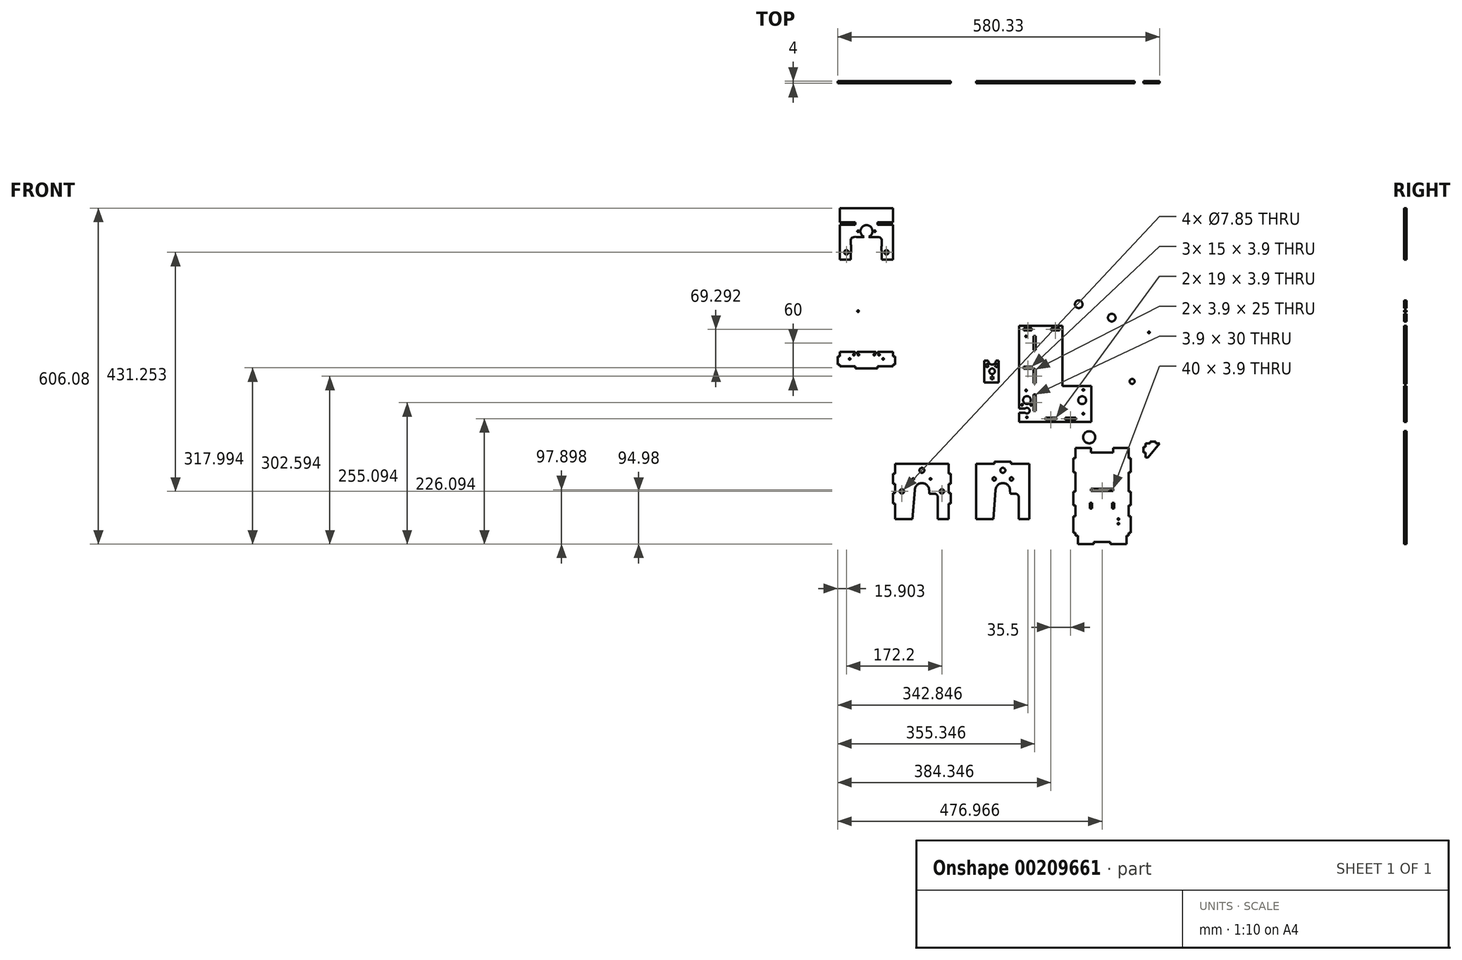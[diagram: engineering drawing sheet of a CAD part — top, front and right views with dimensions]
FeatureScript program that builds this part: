
annotation { "Feature Type Name" : "Feature", "Feature Type Description" : "" }
export const myFeature = defineFeature(function(context is Context, id is Id, definition is map)
    precondition{}
    {
        {
            var Q0;
            Q0=qCreatedBy(makeId("Front.planeOp"),FACE);
            var sketch = newSketch(context, id + "F0", { "sketchPlane" : qUnion([Q0])});
            skLineSegment(sketch, "E0", {"start": v(-63.43, -22.95) * mm, "end": v(-63.43, -82.95) * mm});
            skLineSegment(sketch, "E1", {"start": v(-63.43, -82.95) * mm, "end": v(66.57, -82.95) * mm});
            skLineSegment(sketch, "E2", {"start": v(66.57, -82.95) * mm, "end": v(66.56, -50.54) * mm});
            skLineSegment(sketch, "E3", {"start": v(66.56, -50.54) * mm, "end": v(66.57, -17.95) * mm});
            skLineSegment(sketch, "E4", {"start": v(66.57, -17.95) * mm, "end": v(29.57, -17.95) * mm});
            skLineSegment(sketch, "E5", {"start": v(-37.38, -62.95) * mm, "end": v(-37.38, -32.95) * mm});
            skLineSegment(sketch, "E6", {"start": v(-37.38, -32.95) * mm, "end": v(-33.48, -32.95) * mm});
            skLineSegment(sketch, "E7", {"start": v(-33.48, -32.95) * mm, "end": v(-33.48, -62.95) * mm});
            skLineSegment(sketch, "E8", {"start": v(-33.48, -62.95) * mm, "end": v(-37.38, -62.95) * mm});
            skLineSegment(sketch, "E9", {"start": v(-63.43, -22.95) * mm, "end": v(-63.43, 90.44) * mm});
            skLineSegment(sketch, "E10", {"start": v(-37.38, -12.95) * mm, "end": v(-37.38, 12.05) * mm});
            skLineSegment(sketch, "E11", {"start": v(-37.38, 12.05) * mm, "end": v(-33.48, 12.05) * mm});
            skLineSegment(sketch, "E12", {"start": v(-33.48, 12.05) * mm, "end": v(-33.48, -12.95) * mm});
            skLineSegment(sketch, "E13", {"start": v(-33.48, -12.95) * mm, "end": v(-37.38, -12.95) * mm});
            skLineSegment(sketch, "E14", {"start": v(-63.43, 90.44) * mm, "end": v(14.57, 90.44) * mm});
            skLineSegment(sketch, "E15", {"start": v(9.41, 86.2) * mm, "end": v(9.41, 82.3) * mm});
            skLineSegment(sketch, "E16", {"start": v(9.41, 82.3) * mm, "end": v(-5.59, 82.3) * mm});
            skLineSegment(sketch, "E17", {"start": v(-5.59, 82.3) * mm, "end": v(-5.59, 86.2) * mm});
            skLineSegment(sketch, "E18", {"start": v(-5.59, 86.2) * mm, "end": v(9.41, 86.2) * mm});
            skCircle(sketch, "E19", {"center": v(-50.93, -25.95) * mm, "radius": 1.4 * mm});
            skCircle(sketch, "E20", {"center": v(52.21, -24.95) * mm, "radius": 1.5 * mm});
            skCircle(sketch, "E21", {"center": v(52.21, -67.95) * mm, "radius": 1.5 * mm});
            skCircle(sketch, "E22", {"center": v(-49.43, -74.35) * mm, "radius": 1.4 * mm});
            skLineSegment(sketch, "E23", {"start": v(-40.43, 16.9) * mm, "end": v(-40.43, 13) * mm});
            skLineSegment(sketch, "E24", {"start": v(-40.43, 13) * mm, "end": v(-55.43, 13) * mm});
            skLineSegment(sketch, "E25", {"start": v(-55.43, 13) * mm, "end": v(-55.43, 16.9) * mm});
            skLineSegment(sketch, "E26", {"start": v(-55.43, 16.9) * mm, "end": v(-40.43, 16.9) * mm});
            skLineSegment(sketch, "E27", {"start": v(-37.38, 47.05) * mm, "end": v(-37.38, 72.05) * mm});
            skLineSegment(sketch, "E28", {"start": v(-37.38, 72.05) * mm, "end": v(-33.48, 72.05) * mm});
            skLineSegment(sketch, "E29", {"start": v(-33.48, 72.05) * mm, "end": v(-33.48, 47.05) * mm});
            skLineSegment(sketch, "E30", {"start": v(-33.48, 47.05) * mm, "end": v(-37.38, 47.05) * mm});
            skCircle(sketch, "E31", {"center": v(-50.93, 71.63) * mm, "radius": 1.4 * mm});
            skLineSegment(sketch, "E32", {"start": v(-40.43, 86.2) * mm, "end": v(-40.43, 82.3) * mm});
            skLineSegment(sketch, "E33", {"start": v(-40.43, 82.3) * mm, "end": v(-55.43, 82.3) * mm});
            skLineSegment(sketch, "E34", {"start": v(-55.43, 82.3) * mm, "end": v(-55.43, 86.2) * mm});
            skLineSegment(sketch, "E35", {"start": v(-55.43, 86.2) * mm, "end": v(-40.43, 86.2) * mm});
            skCircle(sketch, "E36", {"center": v(52.21, -24.95) * mm, "radius": 1.4 * mm});
            skCircle(sketch, "E37", {"center": v(52.21, -67.95) * mm, "radius": 1.4 * mm});
            skLineSegment(sketch, "E38", {"start": v(29.57, -17.95) * mm, "end": v(19.57, -17.95) * mm});
            skLineSegment(sketch, "E39", {"start": v(19.57, -17.95) * mm, "end": v(14.57, -17.95) * mm});
            skLineSegment(sketch, "E40", {"start": v(14.57, -17.95) * mm, "end": v(14.57, 90.44) * mm});
            skLineSegment(sketch, "E41", {"start": v(3.07, -78.9) * mm, "end": v(-15.93, -78.9) * mm});
            skLineSegment(sketch, "E42", {"start": v(-15.93, -78.9) * mm, "end": v(-15.93, -75) * mm});
            skLineSegment(sketch, "E43", {"start": v(-15.93, -75) * mm, "end": v(3.07, -75) * mm});
            skLineSegment(sketch, "E44", {"start": v(3.07, -75) * mm, "end": v(3.07, -78.9) * mm});
            skLineSegment(sketch, "E45", {"start": v(38.57, -78.9) * mm, "end": v(19.57, -78.9) * mm});
            skLineSegment(sketch, "E46", {"start": v(19.57, -78.9) * mm, "end": v(19.57, -75) * mm});
            skLineSegment(sketch, "E47", {"start": v(19.57, -75) * mm, "end": v(38.57, -75) * mm});
            skLineSegment(sketch, "E48", {"start": v(38.57, -75) * mm, "end": v(38.57, -78.9) * mm});
            skCircle(sketch, "E49", {"center": v(-49.43, -43.45) * mm, "radius": 7.1 * mm});
            skCircle(sketch, "E50", {"center": v(-49.43, -62.45) * mm, "radius": 5 * mm});
            skLineSegment(sketch, "E51", {"start": v(-52.43, -58.45) * mm, "end": v(-63.43, -58.45) * mm});
            skLineSegment(sketch, "E52", {"start": v(-52.43, -66.45) * mm, "end": v(-63.43, -66.45) * mm});
            skCircle(sketch, "E53", {"center": v(50.08, -43.54) * mm, "radius": 7.1 * mm});
            skCircle(sketch, "E54", {"center": v(-58.5, -51.92) * mm, "radius": 1.4 * mm});
            skCircle(sketch, "E55", {"center": v(-41.8, -51.92) * mm, "radius": 1.4 * mm});
            skSolve(sketch);
        }
        {
            var Q0;
            Q0=qCreatedBy(makeId("Front.planeOp"),FACE);
            var sketch = newSketch(context, id + "F1", { "sketchPlane" : qUnion([Q0])});
            skLineSegment(sketch, "E56", {"start": v(120.16, -22.83) * mm, "end": v(160.16, -22.83) * mm});
            skCircle(sketch, "E57", {"center": v(140.16, -9.68) * mm, "radius": 4.5 * mm});
            skLineSegment(sketch, "E58", {"start": v(115.16, -22.83) * mm, "end": v(165.16, -22.83) * mm});
            skLineSegment(sketch, "E59", {"start": v(165.16, 2.17) * mm, "end": v(162.16, 2.17) * mm});
            skLineSegment(sketch, "E60", {"start": v(118.16, 2.17) * mm, "end": v(115.16, 2.17) * mm});
            skLineSegment(sketch, "E61", {"start": v(120.16, 6.17) * mm, "end": v(160.16, 6.17) * mm});
            skLineSegment(sketch, "E62", {"start": v(115.16, -22.83) * mm, "end": v(115.16, -9.83) * mm});
            skLineSegment(sketch, "E63", {"start": v(120.16, 6.17) * mm, "end": v(120.16, 2.17) * mm});
            skLineSegment(sketch, "E64", {"start": v(160.16, 6.17) * mm, "end": v(160.16, 2.17) * mm});
            skLineSegment(sketch, "E65", {"start": v(118.16, 2.17) * mm, "end": v(120.16, 2.17) * mm});
            skLineSegment(sketch, "E66", {"start": v(162.16, 2.17) * mm, "end": v(160.16, 2.17) * mm});
            skLineSegment(sketch, "E67", {"start": v(115.16, -9.83) * mm, "end": v(115.16, 2.17) * mm});
            skLineSegment(sketch, "E68", {"start": v(115.16, -22.83) * mm, "end": v(115.16, 2.17) * mm});
            skLineSegment(sketch, "E69", {"start": v(165.16, -22.83) * mm, "end": v(165.16, 2.17) * mm});
            skCircle(sketch, "E70", {"center": v(124.99, -15.63) * mm, "radius": 1.4 * mm});
            skCircle(sketch, "E71", {"center": v(155.33, -3.77) * mm, "radius": 1.4 * mm});
            skSolve(sketch);
        }
        {
            var Q0;
            {var subQ5=sQuery(id+"F0.wireOp",EDGE,"E1");Q0=makeQuery(id+"F0.imprint","IMPRINT",FACE,{"disambiguationData":[TD([[makeQuery(id+"F0.imprint","IMPRINT",EDGE,{"derivedFrom":subQ5}),1.0]])]});}
            extrude(context, id + "F2", {"entities" : qUnion([Q0]), "depth" : 4 * mm});
        }
        {
            var Q0;
            Q0=makeQuery(id+"F1.imprint","IMPRINT",FACE,{"disambiguationData":[TD([[makeQuery(id+"F1.imprint","IMPRINT",EDGE,{"derivedFrom":sQuery(id+"F1.wireOp",EDGE,"E57")}),1.0]])]});
            extrude(context, id + "F3", {"entities" : qUnion([Q0]), "depth" : 4 * mm});
        }
        {
            var Q0;
            Q0=qCreatedBy(makeId("Front.planeOp"),FACE);
            var sketch = newSketch(context, id + "F4", { "sketchPlane" : qUnion([Q0])});
            skLineSegment(sketch, "E72", {"start": v(42.9, -98.56) * mm, "end": v(82.9, -98.56) * mm});
            skCircle(sketch, "E73", {"center": v(62.9, -110.41) * mm, "radius": 10.9 * mm});
            skLineSegment(sketch, "E74", {"start": v(42.9, -123.56) * mm, "end": v(82.9, -123.56) * mm});
            skLineSegment(sketch, "E75", {"start": v(37.9, -98.56) * mm, "end": v(87.9, -98.56) * mm});
            skLineSegment(sketch, "E76", {"start": v(37.9, -123.56) * mm, "end": v(87.9, -123.56) * mm});
            skLineSegment(sketch, "E77", {"start": v(37.9, -123.56) * mm, "end": v(37.9, -110.56) * mm});
            skLineSegment(sketch, "E78", {"start": v(87.9, -123.56) * mm, "end": v(87.9, -110.56) * mm});
            skLineSegment(sketch, "E79", {"start": v(41.04, -116.56) * mm, "end": v(44.94, -116.56) * mm});
            skLineSegment(sketch, "E80", {"start": v(44.94, -116.56) * mm, "end": v(44.94, -106.56) * mm});
            skLineSegment(sketch, "E81", {"start": v(44.94, -106.56) * mm, "end": v(41.04, -106.56) * mm});
            skLineSegment(sketch, "E82", {"start": v(41.04, -106.56) * mm, "end": v(41.04, -116.56) * mm});
            skLineSegment(sketch, "E83", {"start": v(87.9, -123.56) * mm, "end": v(87.9, -98.56) * mm});
            skLineSegment(sketch, "E84", {"start": v(37.9, -123.56) * mm, "end": v(37.9, -98.56) * mm});
            skLineSegment(sketch, "E85", {"start": v(84.74, -116.56) * mm, "end": v(80.84, -116.56) * mm});
            skLineSegment(sketch, "E86", {"start": v(80.84, -116.56) * mm, "end": v(80.84, -106.56) * mm});
            skLineSegment(sketch, "E87", {"start": v(80.84, -106.56) * mm, "end": v(84.74, -106.56) * mm});
            skLineSegment(sketch, "E88", {"start": v(84.74, -106.56) * mm, "end": v(84.74, -116.56) * mm});
            skCircle(sketch, "E89", {"center": v(47.72, -116.37) * mm, "radius": 1.4 * mm});
            skCircle(sketch, "E90", {"center": v(78.06, -104.5) * mm, "radius": 1.4 * mm});
            skSolve(sketch);
        }
        {
            var Q0;
            Q0=makeQuery(id+"F4.imprint","IMPRINT",FACE,{"disambiguationData":[TD([[makeQuery(id+"F4.imprint","IMPRINT",EDGE,{"derivedFrom":sQuery(id+"F4.wireOp",EDGE,"E73")}),1.0]])]});
            extrude(context, id + "F5", {"entities" : qUnion([Q0]), "depth" : 4 * mm});
        }
        {
            var Q0;
            Q0=qCreatedBy(makeId("Front.planeOp"),FACE);
            var sketch = newSketch(context, id + "F6", { "sketchPlane" : qUnion([Q0])});
            skLineSegment(sketch, "E91", {"start": v(164.55, -146.61) * mm, "end": v(164.55, -137.73) * mm});
            skLineSegment(sketch, "E92", {"start": v(164.55, -127.73) * mm, "end": v(164.55, -121.73) * mm});
            skLineSegment(sketch, "E93", {"start": v(164.55, -121.73) * mm, "end": v(172.55, -121.73) * mm});
            skLineSegment(sketch, "E94", {"start": v(182.55, -121.73) * mm, "end": v(189.55, -121.73) * mm});
            skLineSegment(sketch, "E95", {"start": v(164.55, -127.73) * mm, "end": v(160.85, -127.73) * mm});
            skLineSegment(sketch, "E96", {"start": v(160.85, -127.73) * mm, "end": v(160.85, -137.73) * mm});
            skLineSegment(sketch, "E97", {"start": v(160.85, -137.73) * mm, "end": v(164.55, -137.73) * mm});
            skLineSegment(sketch, "E98", {"start": v(182.55, -121.73) * mm, "end": v(182.55, -118.03) * mm});
            skLineSegment(sketch, "E99", {"start": v(182.55, -118.03) * mm, "end": v(172.55, -118.03) * mm});
            skLineSegment(sketch, "E100", {"start": v(172.55, -118.03) * mm, "end": v(172.55, -121.73) * mm});
            skLineSegment(sketch, "E101", {"start": v(189.55, -121.73) * mm, "end": v(168.63, -146.61) * mm});
            skLineSegment(sketch, "E102", {"start": v(164.55, -146.61) * mm, "end": v(168.63, -146.61) * mm});
            skSolve(sketch);
        }
        {
            var Q0;
            Q0=makeQuery(id+"F6.imprint","IMPRINT",FACE,{"disambiguationData":[TD([[makeQuery(id+"F6.imprint","IMPRINT",EDGE,{"derivedFrom":sQuery(id+"F6.wireOp",EDGE,"E91")}),-1.0]])]});
            extrude(context, id + "F7", {"entities" : qUnion([Q0]), "depth" : 4 * mm});
        }
        {
            var Q0;
            Q0=qCreatedBy(makeId("Front.planeOp"),FACE);
            var sketch = newSketch(context, id + "F8", { "sketchPlane" : qUnion([Q0])});
            skLineSegment(sketch, "E103", {"start": v(106.19, -129.66) * mm, "end": v(106.19, -137.66) * mm});
            skLineSegment(sketch, "E104", {"start": v(106.19, -137.66) * mm, "end": v(66.19, -137.66) * mm});
            skLineSegment(sketch, "E105", {"start": v(66.19, -137.66) * mm, "end": v(66.19, -129.66) * mm});
            skLineSegment(sketch, "E106", {"start": v(71.19, -303.04) * mm, "end": v(71.19, -299.04) * mm});
            skLineSegment(sketch, "E107", {"start": v(71.19, -299.04) * mm, "end": v(101.19, -299.04) * mm});
            skLineSegment(sketch, "E108", {"start": v(101.19, -299.04) * mm, "end": v(101.19, -303.04) * mm});
            skLineSegment(sketch, "E109", {"start": v(137.89, -283.04) * mm, "end": v(137.89, -253.04) * mm});
            skLineSegment(sketch, "E110", {"start": v(137.89, -253.04) * mm, "end": v(134.19, -253.04) * mm});
            skLineSegment(sketch, "E111", {"start": v(137.89, -283.04) * mm, "end": v(134.19, -283.04) * mm});
            skLineSegment(sketch, "E112", {"start": v(134.19, -129.66) * mm, "end": v(134.19, -148.3) * mm});
            skLineSegment(sketch, "E113", {"start": v(134.19, -173.3) * mm, "end": v(134.19, -208.3) * mm});
            skLineSegment(sketch, "E114", {"start": v(134.19, -233.3) * mm, "end": v(134.19, -253.04) * mm});
            skLineSegment(sketch, "E115", {"start": v(134.19, -283.04) * mm, "end": v(134.19, -288.04) * mm});
            skLineSegment(sketch, "E116", {"start": v(38.19, -129.66) * mm, "end": v(38.19, -148.3) * mm});
            skLineSegment(sketch, "E117", {"start": v(38.19, -173.3) * mm, "end": v(38.19, -208.3) * mm});
            skLineSegment(sketch, "E118", {"start": v(38.19, -233.3) * mm, "end": v(38.19, -253.04) * mm});
            skLineSegment(sketch, "E119", {"start": v(38.19, -283.04) * mm, "end": v(38.19, -288.04) * mm});
            skLineSegment(sketch, "E120", {"start": v(134.19, -129.66) * mm, "end": v(106.19, -129.66) * mm});
            skLineSegment(sketch, "E121", {"start": v(66.19, -129.66) * mm, "end": v(38.19, -129.66) * mm});
            skLineSegment(sketch, "E122", {"start": v(34.49, -283.04) * mm, "end": v(34.49, -253.04) * mm});
            skLineSegment(sketch, "E123", {"start": v(34.49, -253.04) * mm, "end": v(38.19, -253.04) * mm});
            skLineSegment(sketch, "E124", {"start": v(34.49, -283.04) * mm, "end": v(38.19, -283.04) * mm});
            skLineSegment(sketch, "E125", {"start": v(134.19, -283.04) * mm, "end": v(137.89, -283.04) * mm});
            skLineSegment(sketch, "E126", {"start": v(134.19, -233.3) * mm, "end": v(137.89, -233.3) * mm});
            skLineSegment(sketch, "E127", {"start": v(137.89, -233.3) * mm, "end": v(137.89, -208.3) * mm});
            skLineSegment(sketch, "E128", {"start": v(137.89, -208.3) * mm, "end": v(134.19, -208.3) * mm});
            skLineSegment(sketch, "E129", {"start": v(38.19, -233.3) * mm, "end": v(34.49, -233.3) * mm});
            skLineSegment(sketch, "E130", {"start": v(34.49, -233.3) * mm, "end": v(34.49, -208.3) * mm});
            skLineSegment(sketch, "E131", {"start": v(34.49, -208.3) * mm, "end": v(38.19, -208.3) * mm});
            skLineSegment(sketch, "E132", {"start": v(106.19, -215) * mm, "end": v(66.19, -215) * mm});
            skLineSegment(sketch, "E133", {"start": v(66.19, -219.04) * mm, "end": v(106.19, -219.04) * mm});
            skLineSegment(sketch, "E134", {"start": v(130.19, -303.04) * mm, "end": v(101.19, -303.04) * mm});
            skLineSegment(sketch, "E135", {"start": v(71.19, -303.04) * mm, "end": v(42.19, -303.04) * mm});
            skLineSegment(sketch, "E136", {"start": v(134.19, -288.04) * mm, "end": v(130.19, -288.04) * mm});
            skLineSegment(sketch, "E137", {"start": v(130.19, -288.04) * mm, "end": v(130.19, -303.04) * mm});
            skLineSegment(sketch, "E138", {"start": v(64.19, -256.04) * mm, "end": v(64.19, -295.04) * mm});
            skLineSegment(sketch, "E139", {"start": v(64.19, -295.04) * mm, "end": v(108.19, -295.04) * mm});
            skLineSegment(sketch, "E140", {"start": v(108.19, -295.04) * mm, "end": v(108.19, -260.04) * mm});
            skLineSegment(sketch, "E141", {"start": v(108.19, -295.04) * mm, "end": v(108.19, -256.04) * mm});
            skLineSegment(sketch, "E142", {"start": v(104.34, -229.08) * mm, "end": v(96.6, -229.08) * mm});
            skLineSegment(sketch, "E143", {"start": v(74.6, -229.08) * mm, "end": v(68.04, -229.08) * mm});
            skLineSegment(sketch, "E144", {"start": v(96.6, -229.08) * mm, "end": v(74.6, -229.08) * mm});
            skLineSegment(sketch, "E145", {"start": v(68.19, -252.04) * mm, "end": v(68.19, -233.04) * mm});
            skLineSegment(sketch, "E146", {"start": v(108.19, -256.04) * mm, "end": v(104.19, -256.04) * mm});
            skLineSegment(sketch, "E147", {"start": v(104.19, -256.04) * mm, "end": v(104.19, -233.04) * mm});
            skLineSegment(sketch, "E148", {"start": v(38.19, -288.04) * mm, "end": v(42.19, -288.04) * mm});
            skLineSegment(sketch, "E149", {"start": v(42.19, -288.04) * mm, "end": v(42.19, -303.04) * mm});
            skLineSegment(sketch, "E150", {"start": v(108.02, -239.04) * mm, "end": v(104.32, -239.04) * mm});
            skLineSegment(sketch, "E151", {"start": v(104.32, -239.04) * mm, "end": v(104.32, -229.04) * mm});
            skLineSegment(sketch, "E152", {"start": v(104.32, -229.04) * mm, "end": v(108.02, -229.04) * mm});
            skLineSegment(sketch, "E153", {"start": v(108.02, -229.04) * mm, "end": v(108.02, -239.04) * mm});
            skLineSegment(sketch, "E154", {"start": v(64.32, -239.04) * mm, "end": v(68.02, -239.04) * mm});
            skLineSegment(sketch, "E155", {"start": v(68.02, -239.04) * mm, "end": v(68.02, -229.04) * mm});
            skLineSegment(sketch, "E156", {"start": v(68.02, -229.04) * mm, "end": v(64.32, -229.04) * mm});
            skLineSegment(sketch, "E157", {"start": v(64.32, -229.04) * mm, "end": v(64.32, -239.04) * mm});
            skLineSegment(sketch, "E158", {"start": v(106.19, -207.1) * mm, "end": v(106.19, -203.2) * mm});
            skLineSegment(sketch, "E159", {"start": v(106.19, -203.2) * mm, "end": v(66.19, -203.2) * mm});
            skLineSegment(sketch, "E160", {"start": v(66.19, -203.2) * mm, "end": v(66.19, -207.1) * mm});
            skLineSegment(sketch, "E161", {"start": v(66.19, -207.1) * mm, "end": v(106.19, -207.1) * mm});
            skLineSegment(sketch, "E162", {"start": v(106.19, -215) * mm, "end": v(106.19, -219.04) * mm});
            skLineSegment(sketch, "E163", {"start": v(66.19, -215.1) * mm, "end": v(66.19, -219.04) * mm});
            skLineSegment(sketch, "E164", {"start": v(134.19, -173.3) * mm, "end": v(137.89, -173.3) * mm});
            skLineSegment(sketch, "E165", {"start": v(137.89, -173.3) * mm, "end": v(137.89, -148.3) * mm});
            skLineSegment(sketch, "E166", {"start": v(137.89, -148.3) * mm, "end": v(134.19, -148.3) * mm});
            skLineSegment(sketch, "E167", {"start": v(38.19, -173.3) * mm, "end": v(34.49, -173.3) * mm});
            skLineSegment(sketch, "E168", {"start": v(34.49, -173.3) * mm, "end": v(34.49, -148.3) * mm});
            skLineSegment(sketch, "E169", {"start": v(34.49, -148.3) * mm, "end": v(38.19, -148.3) * mm});
            skLineSegment(sketch, "E170", {"start": v(64.19, -256.04) * mm, "end": v(64.19, -252.04) * mm});
            skLineSegment(sketch, "E171", {"start": v(64.19, -252.04) * mm, "end": v(68.19, -252.04) * mm});
            skArc(sketch, "E172", {"start": v(110.44, -264.12) * mm, "mid": v(112.44, -262.12) * mm, "end": v(110.44, -260.12) * mm});
            skLineSegment(sketch, "E173", {"start": v(110.44, -260.12) * mm, "end": v(108.3, -260.12) * mm});
            skLineSegment(sketch, "E174", {"start": v(110.44, -264.12) * mm, "end": v(108.3, -264.12) * mm});
            skCircle(sketch, "E175", {"center": v(115.55, -257.95) * mm, "radius": 1.5 * mm});
            skCircle(sketch, "E176", {"center": v(115.55, -266.3) * mm, "radius": 1.5 * mm});
            skSolve(sketch);
        }
        {
            var Q0;
            Q0=makeQuery(id+"F8.imprint","IMPRINT",FACE,{"disambiguationData":[TD([[makeQuery(id+"F8.imprint","IMPRINT",EDGE,{"derivedFrom":sQuery(id+"F8.wireOp",EDGE,"E103")}),1.0]])]});
            extrude(context, id + "F9", {"entities" : qUnion([Q0]), "depth" : 4 * mm});
        }
        {
            var Q0;
            Q0=qCreatedBy(makeId("Front.planeOp"),FACE);
            var sketch = newSketch(context, id + "F10", { "sketchPlane" : qUnion([Q0])});
            skLineSegment(sketch, "E177", {"start": v(89.47, 65.83) * mm, "end": v(89.47, 140.83) * mm});
            skCircle(sketch, "E178", {"center": v(103.47, 105.32) * mm, "radius": 6.95 * mm});
            skCircle(sketch, "E179", {"center": v(103.47, 74.42) * mm, "radius": 1.4 * mm});
            skLineSegment(sketch, "E180", {"start": v(89.47, 81.33) * mm, "end": v(89.47, 65.83) * mm});
            skLineSegment(sketch, "E181", {"start": v(89.47, 65.83) * mm, "end": v(115.57, 65.83) * mm});
            skLineSegment(sketch, "E182", {"start": v(89.47, 140.83) * mm, "end": v(115.57, 140.83) * mm});
            skCircle(sketch, "E183", {"center": v(101.97, 122.83) * mm, "radius": 1.4 * mm});
            skLineSegment(sketch, "E184", {"start": v(115.57, 65.83) * mm, "end": v(115.57, 140.83) * mm});
            skCircle(sketch, "E185", {"center": v(94.4, 96.85) * mm, "radius": 1.4 * mm});
            skCircle(sketch, "E186", {"center": v(111.1, 96.85) * mm, "radius": 1.4 * mm});
            skLineSegment(sketch, "E187", {"start": v(98.27, 90.32) * mm, "end": v(89.47, 90.32) * mm});
            skLineSegment(sketch, "E188", {"start": v(98.27, 82.32) * mm, "end": v(89.47, 82.32) * mm});
            skLineSegment(sketch, "E189", {"start": v(107.22, 92.82) * mm, "end": v(99.71, 92.82) * mm});
            skLineSegment(sketch, "E190", {"start": v(99.71, 92.82) * mm, "end": v(95.96, 86.32) * mm});
            skLineSegment(sketch, "E191", {"start": v(95.96, 86.32) * mm, "end": v(99.71, 79.82) * mm});
            skLineSegment(sketch, "E192", {"start": v(99.71, 79.82) * mm, "end": v(107.22, 79.82) * mm});
            skLineSegment(sketch, "E193", {"start": v(107.22, 79.82) * mm, "end": v(110.97, 86.32) * mm});
            skLineSegment(sketch, "E194", {"start": v(110.97, 86.32) * mm, "end": v(107.22, 92.82) * mm});
            skSolve(sketch);
        }
        {
            var Q0;
            Q0=makeQuery(id+"F10.imprint","IMPRINT",FACE,{"disambiguationData":[TD([[makeQuery(id+"F10.imprint","IMPRINT",EDGE,{"derivedFrom":sQuery(id+"F10.wireOp",EDGE,"E178")}),1.0]])]});
            extrude(context, id + "F11", {"entities" : qUnion([Q0]), "depth" : 4 * mm});
        }
        {
            var Q0;
            Q0=qCreatedBy(makeId("Front.planeOp"),FACE);
            var sketch = newSketch(context, id + "F12", { "sketchPlane" : qUnion([Q0])});
            skLineSegment(sketch, "E195", {"start": v(106.19, -129.66) * mm, "end": v(106.19, -137.66) * mm});
            skLineSegment(sketch, "E196", {"start": v(106.19, -137.66) * mm, "end": v(66.19, -137.66) * mm});
            skLineSegment(sketch, "E197", {"start": v(66.19, -137.66) * mm, "end": v(66.19, -129.66) * mm});
            skLineSegment(sketch, "E198", {"start": v(71.19, -303.04) * mm, "end": v(71.19, -299.04) * mm});
            skLineSegment(sketch, "E199", {"start": v(71.19, -299.04) * mm, "end": v(101.19, -299.04) * mm});
            skLineSegment(sketch, "E200", {"start": v(101.19, -299.04) * mm, "end": v(101.19, -303.04) * mm});
            skLineSegment(sketch, "E201", {"start": v(137.89, -283.04) * mm, "end": v(137.89, -253.04) * mm});
            skLineSegment(sketch, "E202", {"start": v(137.89, -253.04) * mm, "end": v(134.19, -253.04) * mm});
            skLineSegment(sketch, "E203", {"start": v(137.89, -283.04) * mm, "end": v(134.19, -283.04) * mm});
            skLineSegment(sketch, "E204", {"start": v(134.19, -129.66) * mm, "end": v(134.19, -148.3) * mm});
            skLineSegment(sketch, "E205", {"start": v(134.19, -173.3) * mm, "end": v(134.19, -208.3) * mm});
            skLineSegment(sketch, "E206", {"start": v(134.19, -233.3) * mm, "end": v(134.19, -253.04) * mm});
            skLineSegment(sketch, "E207", {"start": v(134.19, -283.04) * mm, "end": v(134.19, -288.04) * mm});
            skLineSegment(sketch, "E208", {"start": v(38.19, -129.66) * mm, "end": v(38.19, -148.3) * mm});
            skLineSegment(sketch, "E209", {"start": v(38.19, -173.3) * mm, "end": v(38.19, -208.3) * mm});
            skLineSegment(sketch, "E210", {"start": v(38.19, -233.3) * mm, "end": v(38.19, -253.04) * mm});
            skLineSegment(sketch, "E211", {"start": v(38.19, -283.04) * mm, "end": v(38.19, -288.04) * mm});
            skLineSegment(sketch, "E212", {"start": v(134.19, -129.66) * mm, "end": v(106.19, -129.66) * mm});
            skLineSegment(sketch, "E213", {"start": v(66.19, -129.66) * mm, "end": v(38.19, -129.66) * mm});
            skLineSegment(sketch, "E214", {"start": v(34.49, -283.04) * mm, "end": v(34.49, -253.04) * mm});
            skLineSegment(sketch, "E215", {"start": v(34.49, -253.04) * mm, "end": v(38.19, -253.04) * mm});
            skLineSegment(sketch, "E216", {"start": v(34.49, -283.04) * mm, "end": v(38.19, -283.04) * mm});
            skLineSegment(sketch, "E217", {"start": v(134.19, -283.04) * mm, "end": v(137.89, -283.04) * mm});
            skLineSegment(sketch, "E218", {"start": v(134.19, -233.3) * mm, "end": v(137.89, -233.3) * mm});
            skLineSegment(sketch, "E219", {"start": v(137.89, -233.3) * mm, "end": v(137.89, -208.3) * mm});
            skLineSegment(sketch, "E220", {"start": v(137.89, -208.3) * mm, "end": v(134.19, -208.3) * mm});
            skLineSegment(sketch, "E221", {"start": v(38.19, -233.3) * mm, "end": v(34.49, -233.3) * mm});
            skLineSegment(sketch, "E222", {"start": v(34.49, -233.3) * mm, "end": v(34.49, -208.3) * mm});
            skLineSegment(sketch, "E223", {"start": v(34.49, -208.3) * mm, "end": v(38.19, -208.3) * mm});
            skLineSegment(sketch, "E224", {"start": v(106.19, -215) * mm, "end": v(66.19, -215) * mm});
            skLineSegment(sketch, "E225", {"start": v(66.19, -219.04) * mm, "end": v(106.19, -219.04) * mm});
            skLineSegment(sketch, "E226", {"start": v(130.19, -303.04) * mm, "end": v(101.19, -303.04) * mm});
            skLineSegment(sketch, "E227", {"start": v(71.19, -303.04) * mm, "end": v(42.19, -303.04) * mm});
            skLineSegment(sketch, "E228", {"start": v(134.19, -288.04) * mm, "end": v(130.19, -288.04) * mm});
            skLineSegment(sketch, "E229", {"start": v(130.19, -288.04) * mm, "end": v(130.19, -303.04) * mm});
            skLineSegment(sketch, "E230", {"start": v(64.19, -256.04) * mm, "end": v(64.19, -295.04) * mm});
            skLineSegment(sketch, "E231", {"start": v(64.19, -295.04) * mm, "end": v(108.19, -295.04) * mm});
            skLineSegment(sketch, "E232", {"start": v(108.19, -295.04) * mm, "end": v(108.19, -260.04) * mm});
            skLineSegment(sketch, "E233", {"start": v(108.19, -295.04) * mm, "end": v(108.19, -256.04) * mm});
            skLineSegment(sketch, "E234", {"start": v(104.34, -229.08) * mm, "end": v(96.6, -229.08) * mm});
            skLineSegment(sketch, "E235", {"start": v(74.6, -229.08) * mm, "end": v(68.04, -229.08) * mm});
            skLineSegment(sketch, "E236", {"start": v(96.6, -229.08) * mm, "end": v(74.6, -229.08) * mm});
            skLineSegment(sketch, "E237", {"start": v(68.19, -252.04) * mm, "end": v(68.19, -233.04) * mm});
            skLineSegment(sketch, "E238", {"start": v(108.19, -256.04) * mm, "end": v(104.19, -256.04) * mm});
            skLineSegment(sketch, "E239", {"start": v(104.19, -256.04) * mm, "end": v(104.19, -233.04) * mm});
            skLineSegment(sketch, "E240", {"start": v(38.19, -288.04) * mm, "end": v(42.19, -288.04) * mm});
            skLineSegment(sketch, "E241", {"start": v(42.19, -288.04) * mm, "end": v(42.19, -303.04) * mm});
            skLineSegment(sketch, "E242", {"start": v(108.02, -239.04) * mm, "end": v(104.32, -239.04) * mm});
            skLineSegment(sketch, "E243", {"start": v(104.32, -239.04) * mm, "end": v(104.32, -229.04) * mm});
            skLineSegment(sketch, "E244", {"start": v(104.32, -229.04) * mm, "end": v(108.02, -229.04) * mm});
            skLineSegment(sketch, "E245", {"start": v(108.02, -229.04) * mm, "end": v(108.02, -239.04) * mm});
            skLineSegment(sketch, "E246", {"start": v(64.32, -239.04) * mm, "end": v(68.02, -239.04) * mm});
            skLineSegment(sketch, "E247", {"start": v(68.02, -239.04) * mm, "end": v(68.02, -229.04) * mm});
            skLineSegment(sketch, "E248", {"start": v(68.02, -229.04) * mm, "end": v(64.32, -229.04) * mm});
            skLineSegment(sketch, "E249", {"start": v(64.32, -229.04) * mm, "end": v(64.32, -239.04) * mm});
            skLineSegment(sketch, "E250", {"start": v(164.55, -146.61) * mm, "end": v(164.55, -137.73) * mm});
            skLineSegment(sketch, "E251", {"start": v(164.55, -127.73) * mm, "end": v(164.55, -121.73) * mm});
            skLineSegment(sketch, "E252", {"start": v(164.55, -121.73) * mm, "end": v(172.55, -121.73) * mm});
            skLineSegment(sketch, "E253", {"start": v(182.55, -121.73) * mm, "end": v(189.55, -121.73) * mm});
            skLineSegment(sketch, "E254", {"start": v(164.55, -127.73) * mm, "end": v(160.85, -127.73) * mm});
            skLineSegment(sketch, "E255", {"start": v(160.85, -127.73) * mm, "end": v(160.85, -137.73) * mm});
            skLineSegment(sketch, "E256", {"start": v(160.85, -137.73) * mm, "end": v(164.55, -137.73) * mm});
            skLineSegment(sketch, "E257", {"start": v(182.55, -121.73) * mm, "end": v(182.55, -118.03) * mm});
            skLineSegment(sketch, "E258", {"start": v(182.55, -118.03) * mm, "end": v(172.55, -118.03) * mm});
            skLineSegment(sketch, "E259", {"start": v(172.55, -118.03) * mm, "end": v(172.55, -121.73) * mm});
            skLineSegment(sketch, "E260", {"start": v(189.55, -121.73) * mm, "end": v(168.63, -146.61) * mm});
            skLineSegment(sketch, "E261", {"start": v(164.55, -146.61) * mm, "end": v(168.63, -146.61) * mm});
            skLineSegment(sketch, "E262", {"start": v(106.19, -207.1) * mm, "end": v(106.19, -203.2) * mm});
            skLineSegment(sketch, "E263", {"start": v(106.19, -203.2) * mm, "end": v(66.19, -203.2) * mm});
            skLineSegment(sketch, "E264", {"start": v(66.19, -203.2) * mm, "end": v(66.19, -207.1) * mm});
            skLineSegment(sketch, "E265", {"start": v(66.19, -207.1) * mm, "end": v(106.19, -207.1) * mm});
            skLineSegment(sketch, "E266", {"start": v(106.19, -215) * mm, "end": v(106.19, -219.04) * mm});
            skLineSegment(sketch, "E267", {"start": v(66.19, -215.1) * mm, "end": v(66.19, -219.04) * mm});
            skLineSegment(sketch, "E268", {"start": v(134.19, -173.3) * mm, "end": v(137.89, -173.3) * mm});
            skLineSegment(sketch, "E269", {"start": v(137.89, -173.3) * mm, "end": v(137.89, -148.3) * mm});
            skLineSegment(sketch, "E270", {"start": v(137.89, -148.3) * mm, "end": v(134.19, -148.3) * mm});
            skLineSegment(sketch, "E271", {"start": v(38.19, -173.3) * mm, "end": v(34.49, -173.3) * mm});
            skLineSegment(sketch, "E272", {"start": v(34.49, -173.3) * mm, "end": v(34.49, -148.3) * mm});
            skLineSegment(sketch, "E273", {"start": v(34.49, -148.3) * mm, "end": v(38.19, -148.3) * mm});
            skLineSegment(sketch, "E274", {"start": v(64.19, -256.04) * mm, "end": v(64.19, -252.04) * mm});
            skLineSegment(sketch, "E275", {"start": v(64.19, -252.04) * mm, "end": v(68.19, -252.04) * mm});
            skArc(sketch, "E276", {"start": v(110.44, -264.12) * mm, "mid": v(112.44, -262.12) * mm, "end": v(110.44, -260.12) * mm});
            skLineSegment(sketch, "E277", {"start": v(110.44, -260.12) * mm, "end": v(108.3, -260.12) * mm});
            skLineSegment(sketch, "E278", {"start": v(110.44, -264.12) * mm, "end": v(108.3, -264.12) * mm});
            skCircle(sketch, "E279", {"center": v(115.55, -257.95) * mm, "radius": 1.5 * mm});
            skCircle(sketch, "E280", {"center": v(115.55, -266.3) * mm, "radius": 1.5 * mm});
            skLineSegment(sketch, "E281", {"start": v(30.01, 90.02) * mm, "end": v(30.01, 165.02) * mm});
            skCircle(sketch, "E282", {"center": v(44.01, 129.51) * mm, "radius": 6.95 * mm});
            skCircle(sketch, "E283", {"center": v(44.01, 98.6) * mm, "radius": 1.5 * mm});
            skLineSegment(sketch, "E284", {"start": v(30.01, 90.02) * mm, "end": v(60.01, 90.02) * mm});
            skLineSegment(sketch, "E285", {"start": v(30.01, 165.02) * mm, "end": v(56.11, 165.02) * mm});
            skCircle(sketch, "E286", {"center": v(42.51, 147.02) * mm, "radius": 1.4 * mm});
            skLineSegment(sketch, "E287", {"start": v(56.11, 104.52) * mm, "end": v(56.11, 165.02) * mm});
            skLineSegment(sketch, "E288", {"start": v(47.77, 104.01) * mm, "end": v(40.26, 117.01) * mm});
            skCircle(sketch, "E289", {"center": v(34.95, 121.03) * mm, "radius": 1.4 * mm});
            skCircle(sketch, "E290", {"center": v(51.64, 121.03) * mm, "radius": 1.4 * mm});
            skLineSegment(sketch, "E291", {"start": v(38.82, 114.51) * mm, "end": v(30.01, 114.51) * mm});
            skLineSegment(sketch, "E292", {"start": v(38.82, 106.51) * mm, "end": v(30.01, 106.51) * mm});
            skLineSegment(sketch, "E293", {"start": v(60.01, 104.52) * mm, "end": v(56.11, 104.52) * mm});
            skLineSegment(sketch, "E294", {"start": v(60.01, 104.52) * mm, "end": v(60.01, 90.02) * mm});
            skCircle(sketch, "E295", {"center": v(44.01, 110.51) * mm, "radius": 8.5 * mm});
            skSolve(sketch);
        }
        {
            var Q0;
            Q0=makeQuery(id+"F12.imprint","IMPRINT",FACE,{"disambiguationData":[TD([[makeQuery(id+"F12.imprint","IMPRINT",EDGE,{"derivedFrom":sQuery(id+"F12.wireOp",EDGE,"E282")}),1.0]])]});
            extrude(context, id + "F13", {"entities" : qUnion([Q0]), "depth" : 4 * mm});
        }
        {
            var Q0;
            Q0=qCreatedBy(makeId("Front.planeOp"),FACE);
            var sketch = newSketch(context, id + "F14", { "sketchPlane" : qUnion([Q0])});
            skLineSegment(sketch, "E296", {"start": v(156.58, 70.18) * mm, "end": v(156.58, 109.67) * mm});
            skCircle(sketch, "E297", {"center": v(170.58, 78.77) * mm, "radius": 1.4 * mm});
            skLineSegment(sketch, "E298", {"start": v(156.58, 70.18) * mm, "end": v(182.68, 70.18) * mm});
            skLineSegment(sketch, "E299", {"start": v(182.68, 70.18) * mm, "end": v(182.68, 109.67) * mm});
            skCircle(sketch, "E300", {"center": v(170.58, 90.67) * mm, "radius": 5 * mm});
            skCircle(sketch, "E301", {"center": v(161.52, 101.2) * mm, "radius": 1.4 * mm});
            skCircle(sketch, "E302", {"center": v(178.2, 101.2) * mm, "radius": 1.4 * mm});
            skLineSegment(sketch, "E303", {"start": v(156.58, 70.18) * mm, "end": v(156.58, 145.18) * mm});
            skLineSegment(sketch, "E304", {"start": v(156.58, 145.18) * mm, "end": v(182.68, 145.18) * mm});
            skLineSegment(sketch, "E305", {"start": v(182.68, 84.68) * mm, "end": v(182.68, 145.18) * mm});
            skCircle(sketch, "E306", {"center": v(170.58, 109.67) * mm, "radius": 6.95 * mm});
            skCircle(sketch, "E307", {"center": v(169.08, 127.18) * mm, "radius": 1.4 * mm});
            skSolve(sketch);
        }
        {
            var Q0;
            Q0=makeQuery(id+"F14.imprint","IMPRINT",FACE,{"disambiguationData":[TD([[makeQuery(id+"F14.imprint","IMPRINT",EDGE,{"derivedFrom":sQuery(id+"F14.wireOp",EDGE,"E297")}),1.0]])]});
            extrude(context, id + "F15", {"entities" : qUnion([Q0]), "depth" : 4 * mm});
        }
        {
            var Q0;
            Q0=qCreatedBy(makeId("Front.planeOp"),FACE);
            var sketch = newSketch(context, id + "F16", { "sketchPlane" : qUnion([Q0])});
            skLineSegment(sketch, "E308", {"start": v(-126.23, -11.85) * mm, "end": v(-126.23, 27.64) * mm});
            skLineSegment(sketch, "E309", {"start": v(-126.23, -11.85) * mm, "end": v(-100.13, -11.85) * mm});
            skLineSegment(sketch, "E310", {"start": v(-100.13, -11.85) * mm, "end": v(-100.13, 27.64) * mm});
            skCircle(sketch, "E311", {"center": v(-112.23, 8.64) * mm, "radius": 5 * mm});
            skLineSegment(sketch, "E312", {"start": v(-105.28, 27.64) * mm, "end": v(-100.13, 27.64) * mm});
            skLineSegment(sketch, "E313", {"start": v(-119.18, 27.64) * mm, "end": v(-126.23, 27.64) * mm});
            skLineSegment(sketch, "E314", {"start": v(-103.2, 16.72) * mm, "end": v(-106.01, 21.6) * mm});
            skLineSegment(sketch, "E315", {"start": v(-119.89, 16.72) * mm, "end": v(-122.7, 21.6) * mm});
            skLineSegment(sketch, "E316", {"start": v(-110.82, -5.7) * mm, "end": v(-113.64, -0.83) * mm});
            skLineSegment(sketch, "E317", {"start": v(-119.77, 21.8) * mm, "end": v(-122.82, 21.8) * mm});
            skLineSegment(sketch, "E318", {"start": v(-122.82, 21.8) * mm, "end": v(-124.34, 19.16) * mm});
            skLineSegment(sketch, "E319", {"start": v(-124.34, 19.16) * mm, "end": v(-122.82, 16.52) * mm});
            skLineSegment(sketch, "E320", {"start": v(-122.82, 16.52) * mm, "end": v(-119.77, 16.52) * mm});
            skLineSegment(sketch, "E321", {"start": v(-119.77, 16.52) * mm, "end": v(-118.25, 19.16) * mm});
            skLineSegment(sketch, "E322", {"start": v(-118.25, 19.16) * mm, "end": v(-119.77, 21.8) * mm});
            skLineSegment(sketch, "E323", {"start": v(-103.08, 21.8) * mm, "end": v(-106.13, 21.8) * mm});
            skLineSegment(sketch, "E324", {"start": v(-106.13, 21.8) * mm, "end": v(-107.65, 19.16) * mm});
            skLineSegment(sketch, "E325", {"start": v(-107.65, 19.16) * mm, "end": v(-106.13, 16.52) * mm});
            skLineSegment(sketch, "E326", {"start": v(-106.13, 16.52) * mm, "end": v(-103.08, 16.52) * mm});
            skLineSegment(sketch, "E327", {"start": v(-103.08, 16.52) * mm, "end": v(-101.56, 19.16) * mm});
            skLineSegment(sketch, "E328", {"start": v(-101.56, 19.16) * mm, "end": v(-103.08, 21.8) * mm});
            skLineSegment(sketch, "E329", {"start": v(-110.7, -0.63) * mm, "end": v(-113.75, -0.63) * mm});
            skLineSegment(sketch, "E330", {"start": v(-113.75, -0.63) * mm, "end": v(-115.28, -3.27) * mm});
            skLineSegment(sketch, "E331", {"start": v(-115.28, -3.27) * mm, "end": v(-113.75, -5.9) * mm});
            skLineSegment(sketch, "E332", {"start": v(-113.75, -5.9) * mm, "end": v(-110.7, -5.9) * mm});
            skLineSegment(sketch, "E333", {"start": v(-110.7, -5.9) * mm, "end": v(-109.19, -3.27) * mm});
            skLineSegment(sketch, "E334", {"start": v(-109.19, -3.27) * mm, "end": v(-110.7, -0.63) * mm});
            skArc(sketch, "E335", {"start": v(-119.18, 27.64) * mm, "mid": v(-112.23, 20.69) * mm, "end": v(-105.28, 27.64) * mm});
            skSolve(sketch);
        }
        {
            var Q0;
            Q0=makeQuery(id+"F16.imprint","IMPRINT",FACE,{"disambiguationData":[TD([[makeQuery(id+"F16.imprint","IMPRINT",EDGE,{"derivedFrom":sQuery(id+"F16.wireOp",EDGE,"E308")}),-1.0]])]});
            extrude(context, id + "F17", {"entities" : qUnion([Q0]), "depth" : 4 * mm});
        }
        {
            var Q0;
            Q0=qCreatedBy(makeId("Front.planeOp"),FACE);
            var sketch = newSketch(context, id + "F18", { "sketchPlane" : qUnion([Q0])});
            skLineSegment(sketch, "E336", {"start": v(-140.86, -158.2) * mm, "end": v(-140.86, -230.73) * mm});
            skLineSegment(sketch, "E337", {"start": v(-44.86, -158.2) * mm, "end": v(-44.86, -230.73) * mm});
            skArc(sketch, "E338", {"start": v(-79.86, -206.06) * mm, "mid": v(-92.86, -193.06) * mm, "end": v(-105.86, -206.06) * mm});
            skLineSegment(sketch, "E339", {"start": v(-79.87, -205.9) * mm, "end": v(-79.33, -212.31) * mm});
            skLineSegment(sketch, "E340", {"start": v(-77.89, -229.73) * mm, "end": v(-77.8, -230.73) * mm});
            skLineSegment(sketch, "E341", {"start": v(-105.85, -205.9) * mm, "end": v(-110.2, -258.26) * mm});
            skCircle(sketch, "E342", {"center": v(-77.36, -185.56) * mm, "radius": 3 * mm});
            skCircle(sketch, "E343", {"center": v(-108.36, -185.56) * mm, "radius": 3 * mm});
            skLineSegment(sketch, "E344", {"start": v(-77.86, -158.2) * mm, "end": v(-77.86, -154.2) * mm});
            skLineSegment(sketch, "E345", {"start": v(-107.86, -154.2) * mm, "end": v(-107.86, -158.2) * mm});
            skCircle(sketch, "E346", {"center": v(-92.86, -170.06) * mm, "radius": 4.5 * mm});
            skLineSegment(sketch, "E347", {"start": v(-107.86, -154.2) * mm, "end": v(-77.86, -154.2) * mm});
            skLineSegment(sketch, "E348", {"start": v(-64.27, -258.26) * mm, "end": v(-64.27, -218.21) * mm});
            skArc(sketch, "E349", {"start": v(-64.27, -218.21) * mm, "mid": v(-66, -214.04) * mm, "end": v(-70.17, -212.31) * mm});
            skLineSegment(sketch, "E350", {"start": v(-70.17, -212.31) * mm, "end": v(-79.33, -212.31) * mm});
            skLineSegment(sketch, "E351", {"start": v(-140.86, -229.73) * mm, "end": v(-140.86, -258.26) * mm});
            skLineSegment(sketch, "E352", {"start": v(-44.86, -229.73) * mm, "end": v(-44.86, -258.26) * mm});
            skLineSegment(sketch, "E353", {"start": v(-140.86, -258.26) * mm, "end": v(-110.2, -258.26) * mm});
            skLineSegment(sketch, "E354", {"start": v(-64.27, -258.26) * mm, "end": v(-44.86, -258.26) * mm});
            skLineSegment(sketch, "E355", {"start": v(-44.86, -158.2) * mm, "end": v(-77.86, -158.2) * mm});
            skLineSegment(sketch, "E356", {"start": v(-107.86, -158.2) * mm, "end": v(-140.86, -158.2) * mm});
            skSolve(sketch);
        }
        {
            var Q0;
            {var subQ1=sQuery(id+"F18.wireOp",EDGE,"E336");Q0=makeQuery(id+"F18.imprint","IMPRINT",FACE,{"disambiguationData":[TD([[makeQuery(id+"F18.imprint","IMPRINT",EDGE,{"derivedFrom":subQ1}),1.0]])]});}
            extrude(context, id + "F19", {"entities" : qUnion([Q0]), "depth" : 4 * mm});
        }
        {
            var Q0;
            Q0=qCreatedBy(makeId("Front.planeOp"),FACE);
            var sketch = newSketch(context, id + "F20", { "sketchPlane" : qUnion([Q0])});
            skLineSegment(sketch, "E357", {"start": v(-286.78, -194.76) * mm, "end": v(-286.78, -211.26) * mm});
            skArc(sketch, "E358", {"start": v(-225.78, -206.06) * mm, "mid": v(-238.78, -193.06) * mm, "end": v(-251.78, -206.06) * mm});
            skLineSegment(sketch, "E359", {"start": v(-225.78, -205.9) * mm, "end": v(-225.25, -212.31) * mm});
            skLineSegment(sketch, "E360", {"start": v(-251.77, -205.9) * mm, "end": v(-256.12, -258.26) * mm});
            skCircle(sketch, "E361", {"center": v(-223.28, -185.56) * mm, "radius": 1.5 * mm});
            skCircle(sketch, "E362", {"center": v(-254.28, -185.56) * mm, "radius": 1.5 * mm});
            skCircle(sketch, "E363", {"center": v(-238.78, -170.06) * mm, "radius": 4.5 * mm});
            skLineSegment(sketch, "E364", {"start": v(-290.78, -194.76) * mm, "end": v(-290.78, -175.76) * mm});
            skLineSegment(sketch, "E365", {"start": v(-290.78, -175.76) * mm, "end": v(-286.78, -175.76) * mm});
            skCircle(sketch, "E366", {"center": v(-202.68, -208.06) * mm, "radius": 3.92 * mm});
            skCircle(sketch, "E367", {"center": v(-274.88, -208.06) * mm, "radius": 3.92 * mm});
            skLineSegment(sketch, "E368", {"start": v(-286.78, -175.76) * mm, "end": v(-290.78, -175.76) * mm});
            skLineSegment(sketch, "E369", {"start": v(-290.78, -175.76) * mm, "end": v(-290.78, -194.76) * mm});
            skLineSegment(sketch, "E370", {"start": v(-290.78, -194.76) * mm, "end": v(-286.78, -194.76) * mm});
            skLineSegment(sketch, "E371", {"start": v(-290.78, -211.26) * mm, "end": v(-286.78, -211.26) * mm});
            skLineSegment(sketch, "E372", {"start": v(-286.78, -211.26) * mm, "end": v(-290.78, -211.26) * mm});
            skLineSegment(sketch, "E373", {"start": v(-290.78, -211.26) * mm, "end": v(-290.78, -230.26) * mm});
            skLineSegment(sketch, "E374", {"start": v(-190.78, -158.2) * mm, "end": v(-190.78, -175.76) * mm});
            skLineSegment(sketch, "E375", {"start": v(-186.78, -194.76) * mm, "end": v(-186.78, -175.76) * mm});
            skLineSegment(sketch, "E376", {"start": v(-186.78, -175.76) * mm, "end": v(-190.78, -175.76) * mm});
            skLineSegment(sketch, "E377", {"start": v(-190.78, -175.76) * mm, "end": v(-186.78, -175.76) * mm});
            skLineSegment(sketch, "E378", {"start": v(-186.78, -175.76) * mm, "end": v(-186.78, -194.76) * mm});
            skLineSegment(sketch, "E379", {"start": v(-186.78, -194.76) * mm, "end": v(-190.78, -194.76) * mm});
            skLineSegment(sketch, "E380", {"start": v(-186.78, -211.26) * mm, "end": v(-190.78, -211.26) * mm});
            skLineSegment(sketch, "E381", {"start": v(-190.78, -211.26) * mm, "end": v(-186.78, -211.26) * mm});
            skLineSegment(sketch, "E382", {"start": v(-186.78, -211.26) * mm, "end": v(-186.78, -230.26) * mm});
            skLineSegment(sketch, "E383", {"start": v(-210.19, -258.26) * mm, "end": v(-210.19, -218.21) * mm});
            skArc(sketch, "E384", {"start": v(-210.19, -218.21) * mm, "mid": v(-211.92, -214.04) * mm, "end": v(-216.09, -212.31) * mm});
            skLineSegment(sketch, "E385", {"start": v(-216.09, -212.31) * mm, "end": v(-225.25, -212.31) * mm});
            skLineSegment(sketch, "E386", {"start": v(-286.78, -230.26) * mm, "end": v(-286.78, -258.26) * mm});
            skLineSegment(sketch, "E387", {"start": v(-190.78, -230.26) * mm, "end": v(-190.78, -258.26) * mm});
            skLineSegment(sketch, "E388", {"start": v(-186.78, -230.26) * mm, "end": v(-190.78, -230.26) * mm});
            skLineSegment(sketch, "E389", {"start": v(-290.78, -230.26) * mm, "end": v(-286.78, -230.26) * mm});
            skLineSegment(sketch, "E390", {"start": v(-286.78, -258.26) * mm, "end": v(-256.12, -258.26) * mm});
            skLineSegment(sketch, "E391", {"start": v(-210.19, -258.26) * mm, "end": v(-190.78, -258.26) * mm});
            skLineSegment(sketch, "E392", {"start": v(-190.78, -158.2) * mm, "end": v(-286.78, -158.2) * mm});
            skLineSegment(sketch, "E393", {"start": v(-286.78, -158.2) * mm, "end": v(-286.78, -175.76) * mm});
            skLineSegment(sketch, "E394", {"start": v(-190.78, -194.76) * mm, "end": v(-190.78, -211.26) * mm});
            skSolve(sketch);
        }
        {
            var Q0;
            Q0=makeQuery(id+"F20.imprint","IMPRINT",FACE,{"disambiguationData":[TD([[makeQuery(id+"F20.imprint","IMPRINT",EDGE,{"derivedFrom":sQuery(id+"F20.wireOp",EDGE,"E357")}),1.0]])]});
            extrude(context, id + "F21", {"entities" : qUnion([Q0]), "depth" : 4 * mm});
        }
        {
            var Q0;
            Q0=qCreatedBy(makeId("Front.planeOp"),FACE);
            var sketch = newSketch(context, id + "F22", { "sketchPlane" : qUnion([Q0])});
            skLineSegment(sketch, "E395", {"start": v(-386.78, 43.63) * mm, "end": v(-290.78, 43.63) * mm});
            skLineSegment(sketch, "E396", {"start": v(-358.78, 17.63) * mm, "end": v(-386.78, 17.63) * mm});
            skLineSegment(sketch, "E397", {"start": v(-318.78, 17.63) * mm, "end": v(-290.78, 17.63) * mm});
            skLineSegment(sketch, "E398", {"start": v(-290.78, 35.63) * mm, "end": v(-290.78, 43.63) * mm});
            skLineSegment(sketch, "E399", {"start": v(-386.78, 35.63) * mm, "end": v(-386.78, 43.63) * mm});
            skLineSegment(sketch, "E400", {"start": v(-358.78, 13.63) * mm, "end": v(-358.78, 17.63) * mm});
            skLineSegment(sketch, "E401", {"start": v(-318.78, 17.63) * mm, "end": v(-318.78, 13.63) * mm});
            skLineSegment(sketch, "E402", {"start": v(-386.78, 20.63) * mm, "end": v(-386.78, 17.63) * mm});
            skLineSegment(sketch, "E403", {"start": v(-290.78, 20.63) * mm, "end": v(-290.78, 17.63) * mm});
            skLineSegment(sketch, "E404", {"start": v(-318.78, 13.63) * mm, "end": v(-358.78, 13.63) * mm});
            skLineSegment(sketch, "E405", {"start": v(-386.78, 20.63) * mm, "end": v(-390.78, 20.63) * mm});
            skLineSegment(sketch, "E406", {"start": v(-390.78, 20.63) * mm, "end": v(-390.78, 35.63) * mm});
            skLineSegment(sketch, "E407", {"start": v(-390.78, 35.63) * mm, "end": v(-386.78, 35.63) * mm});
            skLineSegment(sketch, "E408", {"start": v(-290.78, 20.63) * mm, "end": v(-286.78, 20.63) * mm});
            skLineSegment(sketch, "E409", {"start": v(-286.78, 20.63) * mm, "end": v(-286.78, 35.63) * mm});
            skLineSegment(sketch, "E410", {"start": v(-286.78, 35.63) * mm, "end": v(-290.78, 35.63) * mm});
            skCircle(sketch, "E411", {"center": v(-368.98, 30.88) * mm, "radius": 1.45 * mm});
            skCircle(sketch, "E412", {"center": v(-308.57, 30.88) * mm, "radius": 1.45 * mm});
            skArc(sketch, "E413", {"start": v(-322.3, 43.63) * mm, "mid": v(-320.3, 41.63) * mm, "end": v(-318.3, 43.63) * mm});
            skCircle(sketch, "E414", {"center": v(-316.13, 38.52) * mm, "radius": 1.5 * mm});
            skCircle(sketch, "E415", {"center": v(-324.47, 38.52) * mm, "radius": 1.5 * mm});
            skArc(sketch, "E416", {"start": v(-359.25, 43.63) * mm, "mid": v(-357.25, 41.63) * mm, "end": v(-355.25, 43.63) * mm});
            skCircle(sketch, "E417", {"center": v(-361.43, 38.52) * mm, "radius": 1.5 * mm});
            skCircle(sketch, "E418", {"center": v(-353.08, 38.52) * mm, "radius": 1.5 * mm});
            skSolve(sketch);
        }
        {
            var Q0;
            Q0=makeQuery(id+"F22.imprint","IMPRINT",FACE,{"disambiguationData":[TD([[makeQuery(id+"F22.imprint","IMPRINT",EDGE,{"derivedFrom":sQuery(id+"F22.wireOp",EDGE,"E396")}),-1.0]])]});
            extrude(context, id + "F23", {"entities" : qUnion([Q0]), "depth" : 4 * mm});
        }
        {
            var Q0;
            Q0=qCreatedBy(makeId("Front.planeOp"),FACE);
            var sketch = newSketch(context, id + "F24", { "sketchPlane" : qUnion([Q0])});
            skLineSegment(sketch, "E419", {"start": v(-292.78, 128.9) * mm, "end": v(-318.78, 128.9) * mm});
            skLineSegment(sketch, "E420", {"start": v(-358.78, 128.9) * mm, "end": v(-384.78, 128.9) * mm});
            skCircle(sketch, "E421", {"center": v(-353.95, 117.05) * mm, "radius": 1.4 * mm});
            skCircle(sketch, "E422", {"center": v(-323.6, 117.05) * mm, "radius": 1.4 * mm});
            skLineSegment(sketch, "E423", {"start": v(-386.78, 128.9) * mm, "end": v(-386.78, 108.9) * mm});
            skLineSegment(sketch, "E424", {"start": v(-290.78, 128.9) * mm, "end": v(-290.78, 108.9) * mm});
            skLineSegment(sketch, "E425", {"start": v(-386.78, 85.9) * mm, "end": v(-390.78, 85.9) * mm});
            skLineSegment(sketch, "E426", {"start": v(-390.78, 85.9) * mm, "end": v(-390.78, 100.9) * mm});
            skLineSegment(sketch, "E427", {"start": v(-390.78, 100.9) * mm, "end": v(-386.78, 100.9) * mm});
            skLineSegment(sketch, "E428", {"start": v(-290.78, 85.9) * mm, "end": v(-286.78, 85.9) * mm});
            skLineSegment(sketch, "E429", {"start": v(-286.78, 85.9) * mm, "end": v(-286.78, 100.9) * mm});
            skLineSegment(sketch, "E430", {"start": v(-286.78, 100.9) * mm, "end": v(-290.78, 100.9) * mm});
            skCircle(sketch, "E431", {"center": v(-338.78, 117.05) * mm, "radius": 4.5 * mm});
            skLineSegment(sketch, "E432", {"start": v(-386.78, 65.9) * mm, "end": v(-290.78, 65.9) * mm});
            skLineSegment(sketch, "E433", {"start": v(-386.78, 65.9) * mm, "end": v(-386.78, 85.9) * mm});
            skLineSegment(sketch, "E434", {"start": v(-386.78, 100.9) * mm, "end": v(-386.78, 128.9) * mm});
            skLineSegment(sketch, "E435", {"start": v(-290.78, 128.9) * mm, "end": v(-290.78, 100.9) * mm});
            skLineSegment(sketch, "E436", {"start": v(-290.78, 85.9) * mm, "end": v(-290.78, 65.9) * mm});
            skCircle(sketch, "E437", {"center": v(-374.88, 79.05) * mm, "radius": 3.92 * mm});
            skCircle(sketch, "E438", {"center": v(-302.68, 79.05) * mm, "radius": 3.92 * mm});
            skLineSegment(sketch, "E439", {"start": v(-311.28, 80.05) * mm, "end": v(-311.28, 65.9) * mm});
            skFitSpline(sketch, "E440", {"points": [v(-311.28, 80.05) * mm, v(-311.76, 88.64) * mm, v(-312.71, 105.74) * mm, v(-329.78, 106.62) * mm, v(-338.28, 107.05) * mm]});
            skLineSegment(sketch, "E441", {"start": v(-290.78, 128.9) * mm, "end": v(-318.78, 128.9) * mm});
            skLineSegment(sketch, "E442", {"start": v(-358.78, 128.9) * mm, "end": v(-386.78, 128.9) * mm});
            skLineSegment(sketch, "E443", {"start": v(-386.78, 128.9) * mm, "end": v(-386.78, 135.9) * mm});
            skLineSegment(sketch, "E444", {"start": v(-290.78, 128.9) * mm, "end": v(-290.78, 135.9) * mm});
            skLineSegment(sketch, "E445", {"start": v(-386.78, 158.9) * mm, "end": v(-290.78, 158.9) * mm});
            skLineSegment(sketch, "E446", {"start": v(-358.78, 132.9) * mm, "end": v(-386.78, 132.9) * mm});
            skLineSegment(sketch, "E447", {"start": v(-318.78, 132.9) * mm, "end": v(-290.78, 132.9) * mm});
            skLineSegment(sketch, "E448", {"start": v(-386.78, 135.9) * mm, "end": v(-390.78, 135.9) * mm});
            skLineSegment(sketch, "E449", {"start": v(-390.78, 135.9) * mm, "end": v(-390.78, 150.9) * mm});
            skLineSegment(sketch, "E450", {"start": v(-390.78, 150.9) * mm, "end": v(-386.78, 150.9) * mm});
            skLineSegment(sketch, "E451", {"start": v(-290.78, 135.9) * mm, "end": v(-286.78, 135.9) * mm});
            skLineSegment(sketch, "E452", {"start": v(-286.78, 135.9) * mm, "end": v(-286.78, 150.9) * mm});
            skLineSegment(sketch, "E453", {"start": v(-286.78, 150.9) * mm, "end": v(-290.78, 150.9) * mm});
            skLineSegment(sketch, "E454", {"start": v(-290.78, 150.9) * mm, "end": v(-290.78, 158.9) * mm});
            skLineSegment(sketch, "E455", {"start": v(-386.78, 150.9) * mm, "end": v(-386.78, 158.9) * mm});
            skLineSegment(sketch, "E456", {"start": v(-358.78, 128.9) * mm, "end": v(-358.78, 132.9) * mm});
            skLineSegment(sketch, "E457", {"start": v(-318.78, 132.9) * mm, "end": v(-318.78, 128.9) * mm});
            skCircle(sketch, "E458", {"center": v(-338.78, 117.05) * mm, "radius": 3 * mm});
            skLineSegment(sketch, "E459", {"start": v(-339.28, 107.05) * mm, "end": v(-338.28, 107.05) * mm});
            skLineSegment(sketch, "E460", {"start": v(-366.78, 80.05) * mm, "end": v(-366.78, 65.9) * mm});
            skFitSpline(sketch, "E461", {"points": [v(-366.78, 80.05) * mm, v(-366.3, 88.64) * mm, v(-365.4, 104.75) * mm, v(-350.2, 106.46) * mm, v(-342.73, 106.9) * mm]});
            skLineSegment(sketch, "E462", {"start": v(-339.28, 107.05) * mm, "end": v(-342.73, 106.9) * mm});
            skSolve(sketch);
        }
        {
            var Q0;
            Q0=makeQuery(id+"F24.imprint","IMPRINT",FACE,{"disambiguationData":[TD([[makeQuery(id+"F24.imprint","IMPRINT",EDGE,{"derivedFrom":sQuery(id+"F24.wireOp",EDGE,"E421")}),1.0]])]});
            extrude(context, id + "F25", {"entities" : qUnion([Q0]), "depth" : 4 * mm});
        }
        {
            var Q0;
            Q0=qCreatedBy(makeId("Front.planeOp"),FACE);
            var sketch = newSketch(context, id + "F26", { "sketchPlane" : qUnion([Q0])});
            skArc(sketch, "E463", {"start": v(-334.89, 251) * mm, "mid": v(-338.74, 272.1) * mm, "end": v(-342.73, 251.03) * mm});
            skLineSegment(sketch, "E464", {"start": v(-292.78, 273.04) * mm, "end": v(-318.78, 273.04) * mm});
            skLineSegment(sketch, "E465", {"start": v(-358.78, 273.04) * mm, "end": v(-384.78, 273.04) * mm});
            skCircle(sketch, "E466", {"center": v(-374.88, 223.2) * mm, "radius": 3.92 * mm});
            skCircle(sketch, "E467", {"center": v(-302.68, 223.2) * mm, "radius": 3.92 * mm});
            skCircle(sketch, "E468", {"center": v(-353.95, 261.2) * mm, "radius": 1.4 * mm});
            skCircle(sketch, "E469", {"center": v(-323.6, 261.2) * mm, "radius": 1.4 * mm});
            skLineSegment(sketch, "E470", {"start": v(-377.78, 210.04) * mm, "end": v(-299.78, 210.04) * mm});
            skLineSegment(sketch, "E471", {"start": v(-386.78, 210.04) * mm, "end": v(-290.78, 210.04) * mm});
            skLineSegment(sketch, "E472", {"start": v(-386.78, 210.04) * mm, "end": v(-386.78, 273.04) * mm});
            skLineSegment(sketch, "E473", {"start": v(-290.78, 273.04) * mm, "end": v(-290.78, 210.04) * mm});
            skLineSegment(sketch, "E474", {"start": v(-366.78, 224.2) * mm, "end": v(-366.78, 210.04) * mm});
            skLineSegment(sketch, "E475", {"start": v(-311.28, 224.2) * mm, "end": v(-311.28, 210.04) * mm});
            skFitSpline(sketch, "E476", {"points": [v(-311.28, 224.2) * mm, v(-311.76, 232.78) * mm, v(-312.65, 248.75) * mm, v(-327.6, 250.57) * mm, v(-334.89, 251) * mm]});
            skFitSpline(sketch, "E477", {"points": [v(-366.78, 224.2) * mm, v(-366.3, 232.78) * mm, v(-365.4, 248.9) * mm, v(-350.2, 250.6) * mm, v(-342.73, 251.03) * mm]});
            skLineSegment(sketch, "E478", {"start": v(-365.78, 210.04) * mm, "end": v(-311.78, 210.04) * mm});
            skLineSegment(sketch, "E479", {"start": v(-358.78, 273.04) * mm, "end": v(-358.78, 277.04) * mm});
            skLineSegment(sketch, "E480", {"start": v(-318.78, 277.04) * mm, "end": v(-318.78, 273.04) * mm});
            skLineSegment(sketch, "E481", {"start": v(-290.78, 273.04) * mm, "end": v(-318.78, 273.04) * mm});
            skLineSegment(sketch, "E482", {"start": v(-358.78, 273.04) * mm, "end": v(-386.78, 273.04) * mm});
            skLineSegment(sketch, "E483", {"start": v(-386.78, 273.04) * mm, "end": v(-386.78, 303.04) * mm});
            skLineSegment(sketch, "E484", {"start": v(-290.78, 273.04) * mm, "end": v(-290.78, 303.04) * mm});
            skLineSegment(sketch, "E485", {"start": v(-386.78, 303.04) * mm, "end": v(-290.78, 303.04) * mm});
            skLineSegment(sketch, "E486", {"start": v(-358.78, 277.04) * mm, "end": v(-386.78, 277.04) * mm});
            skLineSegment(sketch, "E487", {"start": v(-318.78, 277.04) * mm, "end": v(-290.78, 277.04) * mm});
            skCircle(sketch, "E488", {"center": v(-338.78, 261.2) * mm, "radius": 3 * mm});
            skSolve(sketch);
        }
        {
            var Q0;
            Q0=makeQuery(id+"F26.imprint","IMPRINT",FACE,{"disambiguationData":[TD([[makeQuery(id+"F26.imprint","IMPRINT",EDGE,{"derivedFrom":sQuery(id+"F26.wireOp",EDGE,"E463")}),-1.0]])]});
            extrude(context, id + "F27", {"entities" : qUnion([Q0]), "depth" : 4 * mm});
        }
    });
